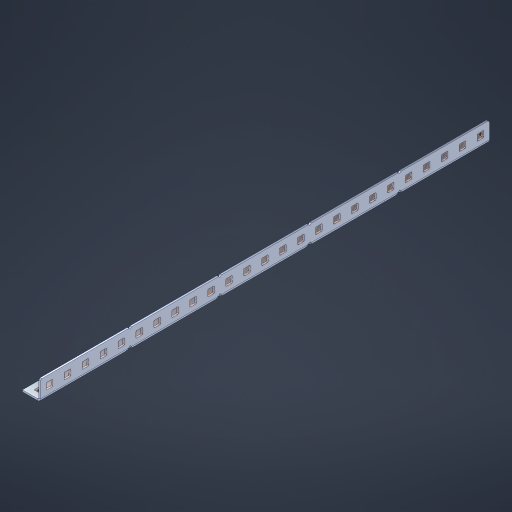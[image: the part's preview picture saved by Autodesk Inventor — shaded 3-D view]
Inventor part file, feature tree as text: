
AUTODESK INVENTOR PART (.ipt)
format: ipt  version: 2023 (Build 270158000, 158)  size: 841,728 bytes
history: native  units: in
note: dims shown in document units (in); Inventor stores cm internally (conversion verified against a paired STEP export)
features: other x55, extrude x49, sheet_metal_op x10, sketch x8, mirror x1, pattern_linear x1, chamfer x1
ambient origin geometry x8: Origin, YZ Plane, XZ Plane, XY Plane, X Axis, Y Axis, Z Axis, Center Point
bodies: Solid1 (feature_tree), Body (feature_tree)
feature tree (125):
  other  "Flange Pattern Plane"
  sheet_metal_op  "Flange Pattern"
  sheet_metal_op  "Body Pattern"
  other  "Arc Length"
  mirror  "Notch Mirror"
  pattern_linear  "Notch Pattern"  Spacing1=0.1875in  [1 undecoded]
  chamfer  "End Chamfer"
  extrude  "Half Cut"  Depth=0.0469in
  sketch  "Sketch1"  dims[d0=2.5in]
  other  "Plate1"
  sketch  "Sketch2"  dims[d1=12.5in]
  other  "Plate2"
  sheet_metal_op  "Bend1"
  sheet_metal_op  "Corner1"
  sketch  "Sketch3"  dims[d2=0.0469in]
  other  "Flange Pattern Sketch"
  sketch  "Sketch7"  dims[d3=0.0469in]
  other  "Srf1"
  other  "Srf2"
  sketch  "Sketch8"  dims[d4=0.0234in]
  sketch  "Sketch9"  dims[d5=0.0938in]
  other  "Srf91"
  sheet_metal_op  "Body Pattern Sketch"
  other  "Srf92"
  sketch  "Sketch13"  dims[d6=0.0469in]
  sketch  "Sketch14"  dims[d7=0.5in d8=90.0deg d9=0.0312in d10=0.1875in d11=0.0469in d12=0.0469in d16=0.182in d17=0.02in d18=0.0469in d19=0.0in d20=0.25in d21=0.25in d46=0.172in d47=1.0in d48=0.0in d49=0.182in d50=0.02in d51=0.25in d52=0.25in d53=0.0469in d54=0.0in d55=0.172in d56=1.0in d57=0.0in d60=9.8425in d62=0.5in d63=0.3937in d65=0.5in d85=0.1227in d86=0.1659in d88=0.04in d89=0.0469in d90=0.0in d91=0.04in d92=0.0491in d95=2.5in d96=0.04in d97=0.25in d98=45.0deg d101=0.0in d102=2.497in d131=0.5in d132=9.8425in d134=0.5in d139=0.5in]
  other  "Srf856"
  other  "Srf1310"
  other  "Srf1311"
  other  "Srf1312"
  other  "Srf1376"
  other  "Srf1377"
  other  "Srf1728"
  other  "Srf1755"
  other  "Srf1878"
  other  "Srf1879"
  other  "Srf1880"
  other  "Srf1881"
  other  "Srf1882"
  other  "Srf1883"
  other  "Srf1884"
  other  "Srf1885"
  other  "Srf1886"
  other  "Srf1887"
  other  "Srf1888"
  other  "Srf1889"
  other  "Srf1890"
  other  "Srf1891"
  other  "Srf1892"
  other  "Srf1893"
  other  "Srf1894"
  other  "Srf1895"
  other  "Srf1896"
  other  "Srf1942"
  other  "Srf1943"
  other  "Srf1944"
  other  "Srf1945"
  other  "Srf1946"
  other  "Srf1947"
  other  "Srf1948"
  other  "Srf1949"
  other  "Srf1950"
  other  "Srf1951"
  other  "Srf1952"
  other  "Srf1953"
  other  "Srf1954"
  other  "Srf1955"
  other  "Srf1956"
  other  "Srf1957"
  other  "Srf1958"
  other  "Srf1959"
  other  "Srf1960"
  sheet_metal_op  "Flange Stamp"
  sheet_metal_op  "Flange Circle"
  sheet_metal_op  "Body Stamp"
  sheet_metal_op  "Body Circle"
  sheet_metal_op  "Notch"
  extrude  "ExtrusionSrf2"  Depth=0.0469in
  extrude  "ExtrusionSrf92"  Depth=0.5in
  extrude  "ExtrusionSrf856"  Depth=0.02in
  extrude  "ExtrusionSrf1310"  Depth=0.0469in
  extrude  "ExtrusionSrf1311"  TaperAngle=0.0deg  [1 undecoded]
  extrude  "ExtrusionSrf1312"  Depth=0.5in
  extrude  "ExtrusionSrf1376"  Depth=0.5in
  extrude  "ExtrusionSrf1377"  Depth=0.5in
  extrude  "ExtrusionSrf1728"  Depth=0.5in TaperAngle=0.0deg
  extrude  "ExtrusionSrf1755"  Depth=0.5in
  extrude  "ExtrusionSrf1878"  Depth=0.02in
  extrude  "ExtrusionSrf1879"  Depth=0.5in
  extrude  "ExtrusionSrf1880"  Depth=0.5in
  extrude  "ExtrusionSrf1881"  Depth=0.0469in
  extrude  "ExtrusionSrf1882"  TaperAngle=0.0deg  [1 undecoded]
  extrude  "ExtrusionSrf1883"  Depth=0.5in
  extrude  "ExtrusionSrf1884"  Depth=0.5in TaperAngle=0.0deg
  extrude  "ExtrusionSrf1885"  Depth=0.5in
  extrude  "ExtrusionSrf1886"  Depth=0.5in
  extrude  "ExtrusionSrf1887"  Depth=0.5in
  extrude  "ExtrusionSrf1888"  Depth=0.5in
  extrude  "ExtrusionSrf1889"  Depth=0.5in
  extrude  "ExtrusionSrf1890"  Depth=0.0469in
  extrude  "ExtrusionSrf1891"  TaperAngle=0.0deg  [1 undecoded]
  extrude  "ExtrusionSrf1892"  Depth=0.5in
  extrude  "ExtrusionSrf1893"  Depth=0.5in
  extrude  "ExtrusionSrf1894"  Depth=0.5in
  extrude  "ExtrusionSrf1895"  Depth=0.5in TaperAngle=45.0deg
  extrude  "ExtrusionSrf1896"  TaperAngle=0.0deg  [1 undecoded]
  extrude  "ExtrusionSrf1942"  Depth=0.5in
  extrude  "ExtrusionSrf1943"  Depth=0.5in
  extrude  "ExtrusionSrf1944"  Depth=0.5in
  extrude  "ExtrusionSrf1945"  Depth=0.5in
  extrude  "ExtrusionSrf1946"  Depth=0.5in
  extrude  "ExtrusionSrf1947"  [1 undecoded]
  extrude  "ExtrusionSrf1948"  [1 undecoded]
  extrude  "ExtrusionSrf1949"  [1 undecoded]
  extrude  "ExtrusionSrf1950"  [1 undecoded]
  extrude  "ExtrusionSrf1951"  [1 undecoded]
  extrude  "ExtrusionSrf1952"  [1 undecoded]
  extrude  "ExtrusionSrf1953"  [1 undecoded]
  extrude  "ExtrusionSrf1954"  [1 undecoded]
  extrude  "ExtrusionSrf1955"  [1 undecoded]
  extrude  "ExtrusionSrf1956"  [1 undecoded]
  extrude  "ExtrusionSrf1957"  [1 undecoded]
  extrude  "ExtrusionSrf1958"  [1 undecoded]
  extrude  "ExtrusionSrf1959"  [1 undecoded]
  extrude  "ExtrusionSrf1960"  [1 undecoded]
note: 19 required parameter values undecoded (feature->parameter linkage not recoverable at this tier; creation-order binding heuristic only, values carry confidence <= 0.55)
